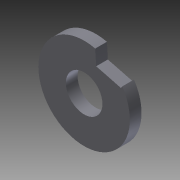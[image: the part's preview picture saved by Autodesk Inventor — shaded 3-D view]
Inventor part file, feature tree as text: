
AUTODESK INVENTOR PART (.ipt)
format: ipt  version: 2014 SP1 (Build 180222100, 222)  size: 89,088 bytes
history: native  units: in
note: dims shown in document units (in); Inventor stores cm internally (conversion verified against a paired STEP export)
features: reference x3, extrude x2, sketch x2
ambient origin geometry x8: Origin, YZ Plane, XZ Plane, XY Plane, X Axis, Y Axis, Z Axis, Center Point
bodies: Solid1 (feature_tree)
feature tree (7):
  extrude  "Extrusion1"  Depth=0.25in
  extrude  "Extrusion2"  Depth=0.08in TaperAngle=0.0deg
  sketch  "Sketch1"  dims[d0=0.625in d1=0.25in]
  sketch  "Sketch2"  dims[d2=0.08in d3=0.0in d4=1.0in d5=0.0in]
  reference  "Reference1"
  reference  "Reference2"
  reference  "Reference3"
